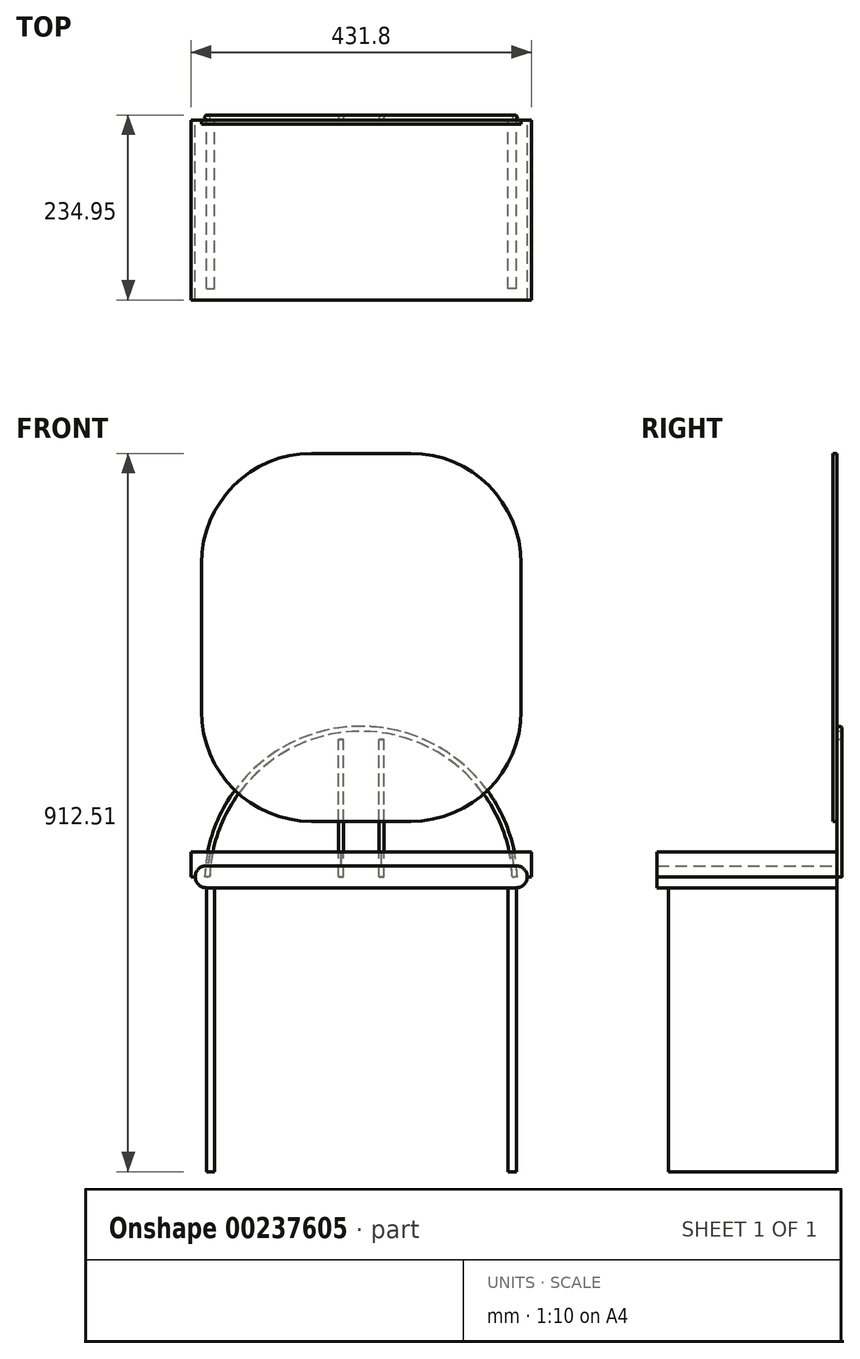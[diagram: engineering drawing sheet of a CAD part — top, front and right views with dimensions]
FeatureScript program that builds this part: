
annotation { "Feature Type Name" : "Feature", "Feature Type Description" : "" }
export const myFeature = defineFeature(function(context is Context, id is Id, definition is map)
    precondition{}
    {
        {
            var Q0;
            Q0=qCreatedBy(makeId("Top.planeOp"),FACE);
            var sketch = newSketch(context, id + "F0", { "sketchPlane" : qUnion([Q0])});
            skLineSegment(sketch, "E0.bottom", {"start": v(215.9, -114.3) * mm, "end": v(-215.9, -114.3) * mm});
            skLineSegment(sketch, "E0.top", {"start": v(215.9, 114.3) * mm, "end": v(-215.9, 114.3) * mm});
            skLineSegment(sketch, "E0.left", {"start": v(215.9, -114.3) * mm, "end": v(215.9, 114.3) * mm});
            skLineSegment(sketch, "E0.right", {"start": v(-215.9, -114.3) * mm, "end": v(-215.9, 114.3) * mm});
            skPoint(sketch, "E0.middle", {"position": v(0, 0) * mm});
            skSolve(sketch);
        }
        {
            var Q0;
            Q0=makeQuery(id+"F0.imprint","IMPRINT",FACE,{"disambiguationData":[TD([[makeQuery(id+"F0.imprint","IMPRINT",EDGE,{"derivedFrom":sQuery(id+"F0.wireOp",EDGE,"E0.bottom")}),-1.0]])]});
            extrude(context, id + "F1", {"entities" : qUnion([Q0]), "depth" : 19.05 * mm});
        }
        {
            var Q0;
            Q0=qCreatedBy(makeId("Front.planeOp"),FACE);
            var sketch = newSketch(context, id + "F2", { "sketchPlane" : qUnion([Q0])});
            skLineSegment(sketch, "E1", {"start": v(0, 0) * mm, "end": v(-196.85, 0) * mm, "construction": true});
            skArc(sketch, "E2", {"start": v(-196.85, 13.97) * mm, "mid": v(-210.82, 0) * mm, "end": v(-196.85, -13.97) * mm});
            skLineSegment(sketch, "E3", {"start": v(-196.85, 0) * mm, "end": v(-196.85, -13.97) * mm, "construction": true});
            skLineSegment(sketch, "E4", {"start": v(-196.85, 0) * mm, "end": v(-196.85, 13.97) * mm, "construction": true});
            skLineSegment(sketch, "E5", {"start": v(-196.85, 13.97) * mm, "end": v(0, 13.97) * mm});
            skLineSegment(sketch, "E6", {"start": v(-196.85, -13.97) * mm, "end": v(0, -13.97) * mm});
            skLineSegment(sketch, "E7.MirrorCS", {"start": v(196.85, 13.97) * mm, "end": v(0, 13.97) * mm});
            skLineSegment(sketch, "E8.MirrorCS", {"start": v(196.85, -13.97) * mm, "end": v(0, -13.97) * mm});
            skArc(sketch, "E9.MirrorCS", {"start": v(196.85, 13.97) * mm, "mid": v(210.82, 0) * mm, "end": v(196.85, -13.97) * mm});
            skSolve(sketch);
        }
        {
            var Q0;
            Q0=makeQuery(id+"F2.imprint","IMPRINT",FACE,{"disambiguationData":[TD([[makeQuery(id+"F2.imprint","IMPRINT",EDGE,{"derivedFrom":sQuery(id+"F2.wireOp",EDGE,"E2")}),1.0]])]});
            extrude(context, id + "F3", {"entities" : qUnion([Q0]), "operationType" : NewBodyOperationType.REMOVE, "endBound" : BoundingType.SYMMETRIC, "depth" : 228.6 * mm});
        }
        {
            var Q0;
            Q0 = qSketchRegion(id + "F2", true);
            extrude(context, id + "F4", {"entities" : qUnion([Q0]), "endBound" : BoundingType.SYMMETRIC, "depth" : 228.6 * mm});
        }
        {
            var Q0;
            Q0=makeQuery(id+"F4.opExtrude","CAP_FACE",FACE,{"disambiguationData":[OSD([sQuery(id+"F2.wireOp",EDGE,"E2"),sQuery(id+"F2.wireOp",EDGE,"E5"),sQuery(id+"F2.wireOp",EDGE,"E6"),sQuery(id+"F2.wireOp",EDGE,"E7.MirrorCS"),sQuery(id+"F2.wireOp",EDGE,"E8.MirrorCS"),sQuery(id+"F2.wireOp",EDGE,"E9.MirrorCS")])],"isStart":true});
            var sketch = newSketch(context, id + "F5", { "sketchPlane" : qUnion([Q0])});
            skLineSegment(sketch, "E10", {"start": v(0, 0) * mm, "end": v(0, 304.12) * mm, "construction": true});
            skLineSegment(sketch, "E11.bottom", {"start": v(-63.2, 70.38) * mm, "end": v(63.2, 70.38) * mm});
            skLineSegment(sketch, "E11.top", {"start": v(-63.2, 537.86) * mm, "end": v(63.2, 537.86) * mm});
            skLineSegment(sketch, "E11.left", {"start": v(-202.9, 210.08) * mm, "end": v(-202.9, 398.16) * mm});
            skLineSegment(sketch, "E11.right", {"start": v(202.9, 210.08) * mm, "end": v(202.9, 398.16) * mm});
            skPoint(sketch, "E11.middle", {"position": v(0, 304.12) * mm});
            skPoint(sketch, "E12.visualSharp", {"position": v(-202.9, 537.86) * mm});
            skArc(sketch, "E12.filletArc", {"start": v(-63.2, 537.86) * mm, "mid": v(-161.98, 496.94) * mm, "end": v(-202.9, 398.16) * mm});
            skPoint(sketch, "E13.visualSharp", {"position": v(202.9, 537.86) * mm});
            skArc(sketch, "E13.filletArc", {"start": v(202.9, 398.16) * mm, "mid": v(161.98, 496.94) * mm, "end": v(63.2, 537.86) * mm});
            skPoint(sketch, "E14.visualSharp", {"position": v(202.9, 70.38) * mm});
            skArc(sketch, "E14.filletArc", {"start": v(63.2, 70.38) * mm, "mid": v(161.98, 111.3) * mm, "end": v(202.9, 210.08) * mm});
            skPoint(sketch, "E15.visualSharp", {"position": v(-202.9, 70.38) * mm});
            skArc(sketch, "E15.filletArc", {"start": v(-202.9, 210.08) * mm, "mid": v(-161.98, 111.3) * mm, "end": v(-63.2, 70.38) * mm});
            skSolve(sketch);
        }
        {
            var Q0;
            Q0=makeQuery(id+"F5.imprint","IMPRINT",FACE,{"disambiguationData":[TD([[makeQuery(id+"F5.imprint","IMPRINT",EDGE,{"derivedFrom":sQuery(id+"F5.wireOp",EDGE,"E11.bottom")}),1.0]])]});
            extrude(context, id + "F6", {"entities" : qUnion([Q0]), "oppositeDirection" : true, "depth" : 5.08 * mm});
        }
        {
            var Q0;
            Q0=makeQuery(id+"F6.opExtrude","CAP_FACE",FACE,{"disambiguationData":[OSD([sQuery(id+"F5.wireOp",EDGE,"E11.bottom"),sQuery(id+"F5.wireOp",EDGE,"E11.top"),sQuery(id+"F5.wireOp",EDGE,"E11.left"),sQuery(id+"F5.wireOp",EDGE,"E11.right"),sQuery(id+"F5.wireOp",EDGE,"E12.filletArc"),sQuery(id+"F5.wireOp",EDGE,"E13.filletArc"),sQuery(id+"F5.wireOp",EDGE,"E14.filletArc"),sQuery(id+"F5.wireOp",EDGE,"E15.filletArc")])],"isStart":true});
            var sketch = newSketch(context, id + "F7", { "sketchPlane" : qUnion([Q0])});
            skArc(sketch, "E16", {"start": v(198.8, 0) * mm, "mid": v(0.34, 191.15) * mm, "end": v(-198.12, 0) * mm});
            skArc(sketch, "E17.0", {"start": v(192.45, -0.24) * mm, "mid": v(0.34, 184.8) * mm, "end": v(-191.78, -0.24) * mm});
            skLineSegment(sketch, "E18", {"start": v(-198.12, 0) * mm, "end": v(-191.78, -0.24) * mm});
            skLineSegment(sketch, "E19", {"start": v(198.8, 0) * mm, "end": v(192.45, -0.24) * mm});
            skLineSegment(sketch, "E20.bottom", {"start": v(-22.35, 0) * mm, "end": v(-28.7, 0) * mm});
            skLineSegment(sketch, "E20.top", {"start": v(-22.35, 174.37) * mm, "end": v(-28.7, 174.37) * mm});
            skLineSegment(sketch, "E20.left", {"start": v(-22.35, 0) * mm, "end": v(-22.35, 174.37) * mm});
            skLineSegment(sketch, "E20.right", {"start": v(-28.7, 0) * mm, "end": v(-28.7, 174.37) * mm});
            skLineSegment(sketch, "E21.MirrorCS", {"start": v(22.35, 0) * mm, "end": v(28.7, 0) * mm});
            skLineSegment(sketch, "E22.MirrorCS", {"start": v(28.7, 0) * mm, "end": v(28.7, 174.37) * mm});
            skLineSegment(sketch, "E23.MirrorCS", {"start": v(22.35, 0) * mm, "end": v(22.35, 174.37) * mm});
            skLineSegment(sketch, "E24.MirrorCS", {"start": v(22.35, 174.37) * mm, "end": v(28.7, 174.37) * mm});
            skSolve(sketch);
        }
        {
            var Q0;
            Q0 = qSketchRegion(id + "F7", true);
            extrude(context, id + "F8", {"entities" : qUnion([Q0]), "depth" : 6.35 * mm});
        }
        {
            var Q0;
            Q0=makeQuery(id+"F8.opExtrude","CAP_EDGE",EDGE,{"disambiguationData":[OSD([sQuery(id+"F7.wireOp",EDGE,"E16")])],"isStart":false});
            var Q1;
            Q1=makeQuery(id+"F8.opExtrude","CAP_EDGE",EDGE,{"disambiguationData":[OSD([sQuery(id+"F7.wireOp",EDGE,"E17.0")])],"isStart":false});
            var Q2;
            Q2=makeQuery(id+"F8.opExtrude","CAP_EDGE",EDGE,{"disambiguationData":[OSD([sQuery(id+"F7.wireOp",EDGE,"E16")])],"isStart":true});
            var Q3;
            Q3=makeQuery(id+"F8.opExtrude","CAP_EDGE",EDGE,{"disambiguationData":[OSD([sQuery(id+"F7.wireOp",EDGE,"E17.0")])],"isStart":true});
            var Q4;
            Q4=makeQuery(id+"F8.opExtrude","CAP_EDGE",EDGE,{"disambiguationData":[OSD([sQuery(id+"F7.wireOp",EDGE,"E20.right")])],"isStart":true});
            var Q5;
            Q5=makeQuery(id+"F8.opExtrude","CAP_EDGE",EDGE,{"disambiguationData":[OSD([sQuery(id+"F7.wireOp",EDGE,"E20.left")])],"isStart":true});
            var Q6;
            Q6=makeQuery(id+"F8.opExtrude","CAP_EDGE",EDGE,{"disambiguationData":[OSD([sQuery(id+"F7.wireOp",EDGE,"E23.MirrorCS")])],"isStart":true});
            var Q7;
            Q7=makeQuery(id+"F8.opExtrude","CAP_EDGE",EDGE,{"disambiguationData":[OSD([sQuery(id+"F7.wireOp",EDGE,"E22.MirrorCS")])],"isStart":true});
            fillet(context, id + "F9", {"entities" : qUnion([Q0, Q1, Q2, Q3, Q4, Q5, Q6, Q7]), "radius" : 3.05 * mm, "tangentPropagation" : true, "allowEdgeOverflow" : false});
        }
        {
            var Q0;
            Q0=makeQuery(id+"F1.opExtrude","CAP_FACE",FACE,{"disambiguationData":[OSD([sQuery(id+"F0.wireOp",EDGE,"E0.bottom"),sQuery(id+"F0.wireOp",EDGE,"E0.top"),sQuery(id+"F0.wireOp",EDGE,"E0.left"),sQuery(id+"F0.wireOp",EDGE,"E0.right")])],"isStart":false});
            extrude(context, id + "F10", {"entities" : qUnion([Q0]), "operationType" : NewBodyOperationType.ADD, "depth" : 12.7 * mm});
        }
        {
            var Q0;
            Q0=makeQuery(id+"F4.opExtrude","SWEPT_FACE",FACE,{"disambiguationData":[OSD([sQuery(id+"F2.wireOp",EDGE,"E6"),sQuery(id+"F2.wireOp",EDGE,"E8.MirrorCS")])]});
            var sketch = newSketch(context, id + "F11", { "sketchPlane" : qUnion([Q0])});
            skLineSegment(sketch, "E25.bottom", {"start": v(-196.85, 100.2) * mm, "end": v(-186.13, 100.2) * mm});
            skLineSegment(sketch, "E25.top", {"start": v(-196.85, -114.3) * mm, "end": v(-186.13, -114.3) * mm});
            skLineSegment(sketch, "E25.left", {"start": v(-196.85, 100.2) * mm, "end": v(-196.85, -114.3) * mm});
            skLineSegment(sketch, "E25.right", {"start": v(-186.13, 100.2) * mm, "end": v(-186.13, -114.3) * mm});
            skLineSegment(sketch, "E26.MirrorCS", {"start": v(196.85, -114.3) * mm, "end": v(186.13, -114.3) * mm});
            skLineSegment(sketch, "E27.MirrorCS", {"start": v(196.85, 100.2) * mm, "end": v(186.13, 100.2) * mm});
            skLineSegment(sketch, "E28.MirrorCS", {"start": v(186.13, 100.2) * mm, "end": v(186.13, -114.3) * mm});
            skLineSegment(sketch, "E29.MirrorCS", {"start": v(196.85, 100.2) * mm, "end": v(196.85, -114.3) * mm});
            skSolve(sketch);
        }
        {
            var Q0;
            Q0 = qSketchRegion(id + "F11", true);
            extrude(context, id + "F12", {"entities" : qUnion([Q0]), "depth" : 360.68 * mm});
        }
    });
